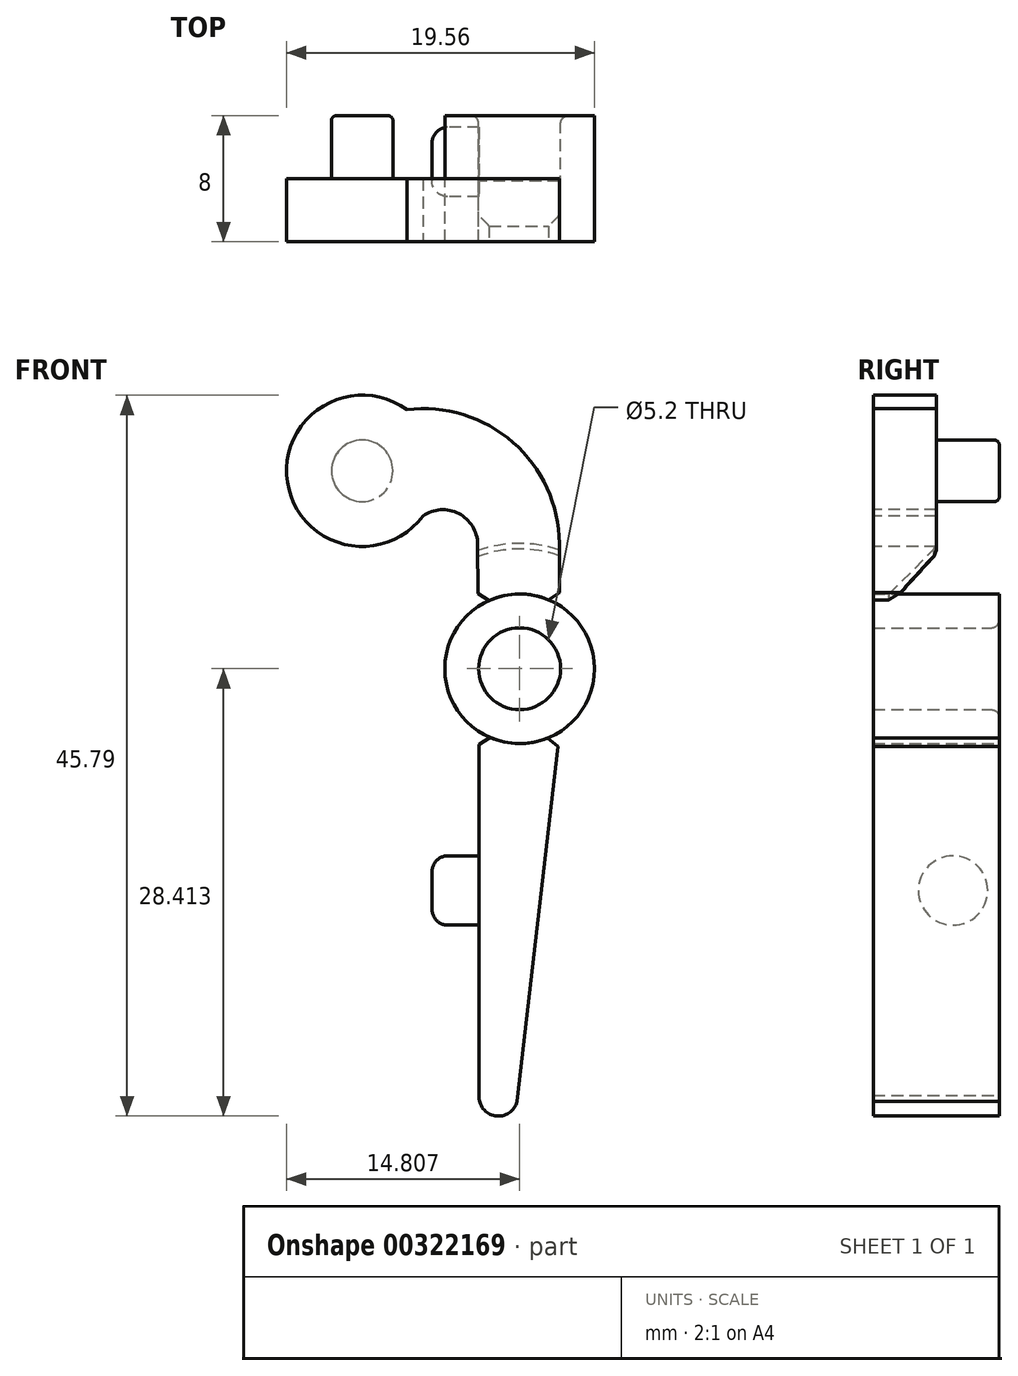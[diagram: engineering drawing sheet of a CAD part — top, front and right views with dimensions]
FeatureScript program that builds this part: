
annotation { "Feature Type Name" : "Feature", "Feature Type Description" : "" }
export const myFeature = defineFeature(function(context is Context, id is Id, definition is map)
    precondition{}
    {
        {
            var Q0;
            Q0=qCreatedBy(makeId("Front.planeOp"),FACE);
            var sketch = newSketch(context, id + "F0", { "sketchPlane" : qUnion([Q0])});
            skCircle(sketch, "E0", {"center": v(5.57, 7.48) * mm, "radius": 2.6 * mm});
            skCircle(sketch, "E1", {"center": v(5.57, 7.48) * mm, "radius": 4.75 * mm});
            skCircle(sketch, "E2", {"center": v(-4.43, 20.06) * mm, "radius": 1.95 * mm});
            skCircle(sketch, "E3", {"center": v(-4.43, 20.06) * mm, "radius": 4.8 * mm});
            skLineSegment(sketch, "E4", {"start": v(8.11, 11.5) * mm, "end": v(8.08, 15.44) * mm});
            skLineSegment(sketch, "E5", {"start": v(2.94, 11.44) * mm, "end": v(2.9, 15.4) * mm});
            skLineSegment(sketch, "E6", {"start": v(3, -4.87) * mm, "end": v(0, -4.87) * mm});
            skLineSegment(sketch, "E7", {"start": v(2.99, -0.47) * mm, "end": v(-0.01, -0.47) * mm});
            skLineSegment(sketch, "E8", {"start": v(-0.01, -0.47) * mm, "end": v(0, -4.87) * mm});
            skLineSegment(sketch, "E9", {"start": v(3, -0.77) * mm, "end": v(7.23, -0.76) * mm});
            skLineSegment(sketch, "E10", {"start": v(3, -4.57) * mm, "end": v(6.8, -4.56) * mm});
            skCircle(sketch, "E11", {"center": v(-4.43, 20.06) * mm, "radius": 1.35 * mm});
            skLineSegment(sketch, "E12", {"start": v(3, -4.87) * mm, "end": v(3, 3.49) * mm, "construction": true});
            skLineSegment(sketch, "E13", {"start": v(3, 3.49) * mm, "end": v(3, -19.6) * mm});
            skArc(sketch, "E14", {"start": v(3, -19.6) * mm, "mid": v(4.02, -20.92) * mm, "end": v(5.4, -20) * mm});
            skLineSegment(sketch, "E15", {"start": v(8.11, 3.47) * mm, "end": v(5.4, -20) * mm});
            skArc(sketch, "E16", {"start": v(2.9, 15.4) * mm, "mid": v(1.7, 17.34) * mm, "end": v(-0.58, 17.19) * mm});
            skArc(sketch, "E17", {"start": v(8.08, 15.44) * mm, "mid": v(5.15, 21.86) * mm, "end": v(-1.6, 23.94) * mm});
            skSolve(sketch);
        }
        {
            var Q0;
            Q0=qCreatedBy(makeId("Right.planeOp"),FACE);
            var sketch = newSketch(context, id + "F1", { "sketchPlane" : qUnion([Q0])});
            skLineSegment(sketch, "E18", {"start": v(0, -14.97) * mm, "end": v(-4, -14.98) * mm});
            skLineSegment(sketch, "E19", {"start": v(0, 14.46) * mm, "end": v(0, -14.97) * mm});
            skLineSegment(sketch, "E20", {"start": v(0, 3.55) * mm, "end": v(-4.07, 3.56) * mm, "construction": true});
            skLineSegment(sketch, "E21", {"start": v(0, 13) * mm, "end": v(-3.98, 13) * mm});
            skLineSegment(sketch, "E22", {"start": v(-4.07, 4.16) * mm, "end": v(0, 4.16) * mm});
            skLineSegment(sketch, "E23", {"start": v(-4.07, 3.56) * mm, "end": v(-8.07, 3.56) * mm});
            skLineSegment(sketch, "E24", {"start": v(-3.98, 13) * mm, "end": v(-7.98, 13) * mm});
            skLineSegment(sketch, "E25", {"start": v(-7.98, 13) * mm, "end": v(-8.07, 3.56) * mm});
            skLineSegment(sketch, "E26", {"start": v(-2.08, 3.56) * mm, "end": v(-2.08, 4.16) * mm});
            skLineSegment(sketch, "E27", {"start": v(-4, -14.98) * mm, "end": v(-4, 3.56) * mm});
            skLineSegment(sketch, "E28", {"start": v(0.01, 14.46) * mm, "end": v(-1.99, 14.46) * mm});
            skLineSegment(sketch, "E29", {"start": v(0, 14.46) * mm, "end": v(0, 13) * mm});
            skLineSegment(sketch, "E30", {"start": v(0, 13) * mm, "end": v(0, 4.74) * mm, "construction": true});
            skLineSegment(sketch, "E31", {"start": v(-1.99, 4.74) * mm, "end": v(0, 4.74) * mm, "construction": true});
            skLineSegment(sketch, "E32", {"start": v(-1.98, 11.5) * mm, "end": v(-6.2, 11.5) * mm, "construction": true});
            skLineSegment(sketch, "E33", {"start": v(-6.2, 11.5) * mm, "end": v(-6.2, 7.6) * mm, "construction": true});
            skLineSegment(sketch, "E34", {"start": v(-1.99, 7.6) * mm, "end": v(-6.2, 7.6) * mm, "construction": true});
            skLineSegment(sketch, "E35", {"start": v(-6.19, 10.8) * mm, "end": v(-1.99, 10.8) * mm, "construction": true});
            skLineSegment(sketch, "E36", {"start": v(-1.99, 10.8) * mm, "end": v(0, 10.8) * mm, "construction": true});
            skLineSegment(sketch, "E37", {"start": v(-8.05, 5.83) * mm, "end": v(0, 5.76) * mm, "construction": true});
            skLineSegment(sketch, "E38", {"start": v(-6.19, 10.8) * mm, "end": v(-8, 10.8) * mm, "construction": true});
            skCircle(sketch, "E39", {"center": v(-2.93, -6.6) * mm, "radius": 2.2 * mm});
            skLineSegment(sketch, "E40", {"start": v(0, 0.17) * mm, "end": v(-3.59, 0.18) * mm, "construction": true});
            skLineSegment(sketch, "E41", {"start": v(0, -4.2) * mm, "end": v(-3.83, -4.22) * mm, "construction": true});
            skLineSegment(sketch, "E42", {"start": v(-2.06, -0.12) * mm, "end": v(-3.56, -0.12) * mm, "construction": true});
            skLineSegment(sketch, "E43", {"start": v(-2.05, -3.92) * mm, "end": v(-3.86, -3.92) * mm, "construction": true});
            skLineSegment(sketch, "E44", {"start": v(-3.3, 0.18) * mm, "end": v(-3.3, -0.12) * mm});
            skLineSegment(sketch, "E45", {"start": v(-3.13, -3.92) * mm, "end": v(-3.12, -4.22) * mm});
            skLineSegment(sketch, "E46", {"start": v(-1.99, 10.56) * mm, "end": v(-6.2, 10.56) * mm, "construction": true});
            skLineSegment(sketch, "E47", {"start": v(-1.99, 8.57) * mm, "end": v(-6.2, 8.57) * mm, "construction": true});
            skLineSegment(sketch, "E48", {"start": v(-6.2, 14.44) * mm, "end": v(-6.2, 11.5) * mm, "construction": true});
            skLineSegment(sketch, "E49", {"start": v(-6.2, 14.44) * mm, "end": v(-1.99, 14.46) * mm, "construction": true});
            skLineSegment(sketch, "E50", {"start": v(0, 16.08) * mm, "end": v(0, -18.09) * mm, "construction": true});
            skLineSegment(sketch, "E51", {"start": v(-1.99, 14.46) * mm, "end": v(-1.99, -14.97) * mm, "construction": true});
            skLineSegment(sketch, "E52", {"start": v(0, 8.2) * mm, "end": v(3.73, 8.2) * mm, "construction": true});
            skLineSegment(sketch, "E53", {"start": v(-2.93, -6.6) * mm, "end": v(4.2, -6.6) * mm, "construction": true});
            skCircle(sketch, "E54", {"center": v(-1.99, 3.16) * mm, "radius": 1 * mm});
            skSolve(sketch);
        }
        {
            var Q0;
            {var subQ0=sQuery(id+"F0.wireOp",EDGE,"E14");Q0=makeQuery(id+"F0.imprint","IMPRINT",FACE,{"disambiguationData":[TD([[makeQuery(id+"F0.imprint","IMPRINT",EDGE,{"derivedFrom":subQ0}),1.0]])]});}
            extrude(context, id + "F2", {"entities" : qUnion([Q0]), "depth" : 8 * mm});
        }
        {
            var Q0;
            Q0=makeQuery(id+"F0.imprint","IMPRINT",FACE,{"disambiguationData":[TD([[makeQuery(id+"F0.imprint","IMPRINT",EDGE,{"derivedFrom":sQuery(id+"F0.wireOp",EDGE,"E2")}),1.0]])]});
            var Q1;
            Q1=makeQuery(id+"F0.imprint","IMPRINT",FACE,{"disambiguationData":[TD([[makeQuery(id+"F0.imprint","IMPRINT",EDGE,{"derivedFrom":sQuery(id+"F0.wireOp",EDGE,"E11")}),1.0]])]});
            extrude(context, id + "F3", {"entities" : qUnion([Q0, Q1]), "operationType" : NewBodyOperationType.ADD, "depth" : 8 * mm});
        }
        {
            var Q0;
            Q0=makeQuery(id+"F0.imprint","IMPRINT",FACE,{"disambiguationData":[TD([[makeQuery(id+"F0.imprint","IMPRINT",EDGE,{"derivedFrom":sQuery(id+"F0.wireOp",EDGE,"E0")}),-1.0]])]});
            extrude(context, id + "F4", {"entities" : qUnion([Q0]), "depth" : 8 * mm});
        }
        {
            var Q0;
            {var subQ0=sQuery(id+"F1.wireOp",EDGE,"E39");var subQ1=sQuery(id+"F1.wireOp",EDGE,"E27");var subQ2=makeQuery(id+"F1.imprint","INTERSECT",VERTEX,{"disambiguationData":[OD(0.0)],"derivedFrom":[subQ1,subQ0]});Q0=makeQuery(id+"F1.imprint","IMPRINT",FACE,{"disambiguationData":[TD([[makeQuery(id+"F1.imprint","IMPRINT",EDGE,{"disambiguationData":[TD([[subQ2,-1.0]])],"derivedFrom":subQ1}),1.0]])]});}
            var Q1;
            {var subQ0=sQuery(id+"F1.wireOp",EDGE,"E39");var subQ1=sQuery(id+"F1.wireOp",EDGE,"E27");var subQ2=makeQuery(id+"F1.imprint","INTERSECT",VERTEX,{"disambiguationData":[OD(0.0)],"derivedFrom":[subQ1,subQ0]});Q1=makeQuery(id+"F1.imprint","IMPRINT",FACE,{"disambiguationData":[TD([[makeQuery(id+"F1.imprint","IMPRINT",EDGE,{"disambiguationData":[TD([[subQ2,-1.0]])],"derivedFrom":subQ1}),-1.0]])]});}
            extrude(context, id + "F5", {"entities" : qUnion([Q0, Q1]), "operationType" : NewBodyOperationType.ADD, "depth" : 6.2 * mm});
        }
        {
            var Q0;
            Q0=makeQuery(id+"F5.opExtrude","CAP_EDGE",EDGE,{"disambiguationData":[OSD([sQuery(id+"F1.wireOp",EDGE,"E39")])],"isStart":true});
            fillet(context, id + "F6", {"entities" : qUnion([Q0]), "radius" : 1 * mm, "tangentPropagation" : true, "allowEdgeOverflow" : false});
        }
        {
            var Q0;
            Q0=makeQuery(id+"F0.imprint","IMPRINT",FACE,{"disambiguationData":[TD([[makeQuery(id+"F0.imprint","IMPRINT",EDGE,{"derivedFrom":sQuery(id+"F0.wireOp",EDGE,"E2")}),-1.0]])]});
            var Q1;
            {var subQ0=sQuery(id+"F0.wireOp",EDGE,"E4");Q1=makeQuery(id+"F0.imprint","IMPRINT",FACE,{"disambiguationData":[TD([[makeQuery(id+"F0.imprint","IMPRINT",EDGE,{"derivedFrom":subQ0}),1.0]])]});}
            var Q2;
            Q2=makeQuery(id+"F3.opExtrude","SWEPT_BODY",BODY,{"disambiguationData":[OSD([sQuery(id+"F0.wireOp",EDGE,"E2"),sQuery(id+"F0.wireOp",EDGE,"E11")])]});
            var Q3;
            Q3=sQuery(id+"F1.wireOp",VERTEX,"E47.end");
            extrude(context, id + "F7", {"entities" : qUnion([Q0, Q1]), "endBoundEntityBody" : qUnion([Q2]), "endBoundEntityVertex" : qUnion([Q3]), "depth" : 4 * mm});
        }
        {
            var Q0;
            Q0=makeQuery(id+"F3.opExtrude","SWEPT_BODY",BODY,{"disambiguationData":[OSD([sQuery(id+"F0.wireOp",EDGE,"E2"),sQuery(id+"F0.wireOp",EDGE,"E11")])]});
            var Q1;
            Q1=makeQuery(id+"F7.opExtrude","SWEPT_BODY",BODY,{"disambiguationData":[OSD([sQuery(id+"F0.wireOp",EDGE,"E11")])]});
            var Q2;
            Q2=makeQuery(id+"F7.opExtrude","SWEPT_BODY",BODY,{"disambiguationData":[OSD([sQuery(id+"F0.wireOp",EDGE,"E1"),sQuery(id+"F0.wireOp",EDGE,"E2"),sQuery(id+"F0.wireOp",EDGE,"E3"),sQuery(id+"F0.wireOp",EDGE,"E4"),sQuery(id+"F0.wireOp",EDGE,"E5")])]});
            booleanBodies(context, id + "F8", {"operationType" : BooleanOperationType.UNION, "tools" : qUnion([Q0, Q1, Q2])});
        }
        {
            var Q0;
            Q0=makeQuery(id+"F3.opExtrude","SWEPT_BODY",BODY,{"disambiguationData":[OSD([sQuery(id+"F0.wireOp",EDGE,"E2"),sQuery(id+"F0.wireOp",EDGE,"E11")])]});
            transform(context, id + "F9", {"entities" : qUnion([Q0]), "transformType" : TransformType.TRANSLATION_3D, "dx" : 0 * mm, "dy" : -10 * mm, "dz" : 0 * mm, "makeCopy" : false});
        }
        {
            var Q0;
            Q0=makeQuery(id+"F3.opExtrude","SWEPT_BODY",BODY,{"disambiguationData":[OSD([sQuery(id+"F0.wireOp",EDGE,"E2"),sQuery(id+"F0.wireOp",EDGE,"E11")])]});
            var Q1;
            {var subQ0=sQuery(id+"F0.wireOp",EDGE,"E11");var subQ1=sQuery(id+"F0.wireOp",EDGE,"E2");Q1=makeQuery(id+"F8.opBoolean","MERGE",FACE,{"derivedFrom":[makeQuery(id+"F3.opExtrude","CAP_FACE",FACE,{"disambiguationData":[OSD([subQ1,subQ0])],"isStart":true}),makeQuery(id+"F7.opExtrude","CAP_FACE",FACE,{"disambiguationData":[OSD([sQuery(id+"F0.wireOp",EDGE,"E1"),subQ1,sQuery(id+"F0.wireOp",EDGE,"E3"),sQuery(id+"F0.wireOp",EDGE,"E4"),sQuery(id+"F0.wireOp",EDGE,"E5")])],"isStart":true}),makeQuery(id+"F7.opExtrude","CAP_FACE",FACE,{"disambiguationData":[OSD([subQ0])],"isStart":true})]});}
            mirror(context, id + "F10", {"entities" : qUnion([Q0]), "mirrorPlane" : qUnion([Q1])});
        }
        {
            var Q0;
            Q0=makeQuery(id+"F3.opExtrude","SWEPT_BODY",BODY,{"disambiguationData":[OSD([sQuery(id+"F0.wireOp",EDGE,"E2"),sQuery(id+"F0.wireOp",EDGE,"E11")])]});
            deleteBodies(context, id + "F11", {"entities" : qUnion([Q0])});
        }
        {
            var Q0;
            Q0=makeQuery(id+"F10.opPattern","COPY",BODY,{"derivedFrom":makeQuery(id+"F3.opExtrude","SWEPT_BODY",BODY,{"disambiguationData":[OSD([sQuery(id+"F0.wireOp",EDGE,"E2"),sQuery(id+"F0.wireOp",EDGE,"E11")])]}),"instanceName":"1"});
            transform(context, id + "F12", {"entities" : qUnion([Q0]), "transformType" : TransformType.TRANSLATION_3D, "dx" : 0 * mm, "dy" : 2 * mm, "dz" : 0 * mm, "makeCopy" : false});
        }
        {
            var Q0;
            Q0=makeQuery(id+"F10.opPattern","COPY",EDGE,{"derivedFrom":makeQuery(id+"F7.opExtrude","CAP_EDGE",EDGE,{"disambiguationData":[OSD([sQuery(id+"F0.wireOp",EDGE,"E1")])],"isStart":false}),"instanceName":"1"});
            chamfer(context, id + "F13", {"entities" : qUnion([Q0]), "width" : 3 * mm, "tangentPropagation" : true});
        }
        {
            var Q0;
            Q0=makeQuery(id+"F4.opExtrude","CAP_EDGE",EDGE,{"disambiguationData":[OSD([sQuery(id+"F0.wireOp",EDGE,"E0")])],"isStart":true});
            fillet(context, id + "F14", {"entities" : qUnion([Q0]), "radius" : 0.5 * mm, "tangentPropagation" : true, "allowEdgeOverflow" : false});
        }
        {
            var Q0;
            Q0=makeQuery(id+"F2.opExtrude","SWEPT_EDGE",EDGE,{"disambiguationData":[OSD([sQuery(id+"F0.wireOp",EDGE,"E1"),sQuery(id+"F0.wireOp",EDGE,"E13")])]});
            var Q1;
            Q1=makeQuery(id+"F10.opPattern","COPY",EDGE,{"derivedFrom":makeQuery(id+"F7.opExtrude","SWEPT_EDGE",EDGE,{"disambiguationData":[OSD([sQuery(id+"F0.wireOp",EDGE,"E1"),sQuery(id+"F0.wireOp",EDGE,"E5")])]}),"instanceName":"1"});
            var Q2;
            {var subQ0=sQuery(id+"F0.wireOp",EDGE,"E1");Q2=makeQuery(id+"F13.opChamfer","BLEND_EDGE",EDGE,{"blendedFrom":[makeQuery(id+"F10.opPattern","COPY",EDGE,{"derivedFrom":makeQuery(id+"F7.opExtrude","CAP_EDGE",EDGE,{"disambiguationData":[OSD([subQ0])],"isStart":false}),"instanceName":"1"}),makeQuery(id+"F4.opExtrude","SWEPT_FACE",FACE,{"disambiguationData":[OSD([subQ0])]})],"blendedInto":[makeQuery(id+"F4.opExtrude","SWEPT_FACE",FACE,{"disambiguationData":[OSD([subQ0])]})]});}
            var Q3;
            {var subQ0=sQuery(id+"F0.wireOp",EDGE,"E1");Q3=makeQuery(id+"F13.opChamfer","BLEND_EDGE",EDGE,{"blendedFrom":[makeQuery(id+"F10.opPattern","COPY",EDGE,{"derivedFrom":makeQuery(id+"F7.opExtrude","CAP_EDGE",EDGE,{"disambiguationData":[OSD([subQ0])],"isStart":false}),"instanceName":"1"}),makeQuery(id+"F10.opPattern","COPY",FACE,{"derivedFrom":makeQuery(id+"F7.opExtrude","CAP_FACE",FACE,{"disambiguationData":[OSD([subQ0,sQuery(id+"F0.wireOp",EDGE,"E2"),sQuery(id+"F0.wireOp",EDGE,"E3"),sQuery(id+"F0.wireOp",EDGE,"E4"),sQuery(id+"F0.wireOp",EDGE,"E5"),sQuery(id+"F0.wireOp",EDGE,"2044f696-4e0a-41ef-984f-ca4b16aea0ce"),sQuery(id+"F0.wireOp",EDGE,"303af563-ceaa-4c7b-aefa-f6317eac3b22")])],"isStart":false}),"instanceName":"1"})],"blendedInto":[makeQuery(id+"F10.opPattern","COPY",FACE,{"derivedFrom":makeQuery(id+"F7.opExtrude","CAP_FACE",FACE,{"disambiguationData":[OSD([subQ0,sQuery(id+"F0.wireOp",EDGE,"E2"),sQuery(id+"F0.wireOp",EDGE,"E3"),sQuery(id+"F0.wireOp",EDGE,"E4"),sQuery(id+"F0.wireOp",EDGE,"E5"),sQuery(id+"F0.wireOp",EDGE,"2044f696-4e0a-41ef-984f-ca4b16aea0ce"),sQuery(id+"F0.wireOp",EDGE,"303af563-ceaa-4c7b-aefa-f6317eac3b22")])],"isStart":false}),"instanceName":"1"})]});}
            var Q4;
            Q4=makeQuery(id+"F10.opPattern","COPY",EDGE,{"derivedFrom":makeQuery(id+"F7.opExtrude","SWEPT_EDGE",EDGE,{"disambiguationData":[OSD([sQuery(id+"F0.wireOp",EDGE,"E1"),sQuery(id+"F0.wireOp",EDGE,"E4")])]}),"instanceName":"1"});
            var Q5;
            Q5=makeQuery(id+"F2.opExtrude","SWEPT_EDGE",EDGE,{"disambiguationData":[OSD([sQuery(id+"F0.wireOp",EDGE,"E1"),sQuery(id+"F0.wireOp",EDGE,"E15")])]});
            chamfer(context, id + "F15", {"entities" : qUnion([Q0, Q1, Q2, Q3, Q4, Q5]), "width" : 0.5 * mm, "tangentPropagation" : true});
        }
        {
            var Q0;
            Q0=makeQuery(id+"F10.opPattern","COPY",EDGE,{"derivedFrom":makeQuery(id+"F3.opExtrude","CAP_EDGE",EDGE,{"disambiguationData":[OSD([sQuery(id+"F0.wireOp",EDGE,"E2")])],"isStart":false}),"instanceName":"1"});
            fillet(context, id + "F16", {"entities" : qUnion([Q0]), "radius" : 0.3 * mm, "tangentPropagation" : true, "allowEdgeOverflow" : false});
        }
    });
